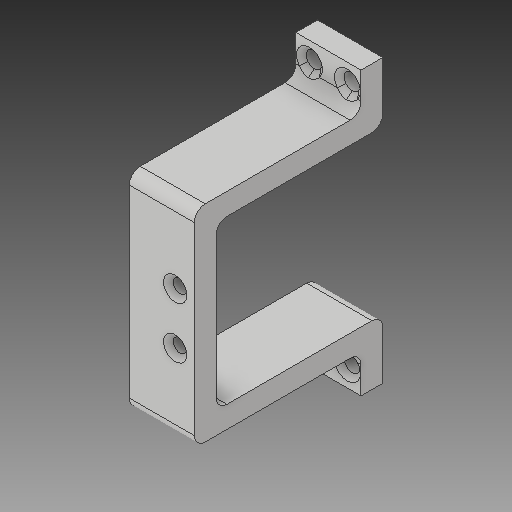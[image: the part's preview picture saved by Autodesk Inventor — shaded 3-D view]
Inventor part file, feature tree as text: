
AUTODESK INVENTOR PART (.ipt)
format: ipt  version: 2019 (Build 230136000, 136)  size: 208,384 bytes
history: native  units: mm
features: sketch x4, other x3, plane x2
ambient origin geometry x8: Origin, YZ Plane, XZ Plane, XY Plane, X Axis, Y Axis, Z Axis, Center Point
bodies: Solid1 (feature_tree)
feature tree (9):
  other  "Endstop_holder.ipt"
  other  "Solid1::Endstop_holder.ipt"
  other  "TaggingFeature1"
  sketch  "Sketch1"  dims[d0=10.0mm]
  sketch  "Sketch2"
  sketch  "Sketch3"
  sketch  "Sketch4"
  plane  "Work Plane1"
  plane  "Work Plane2"
